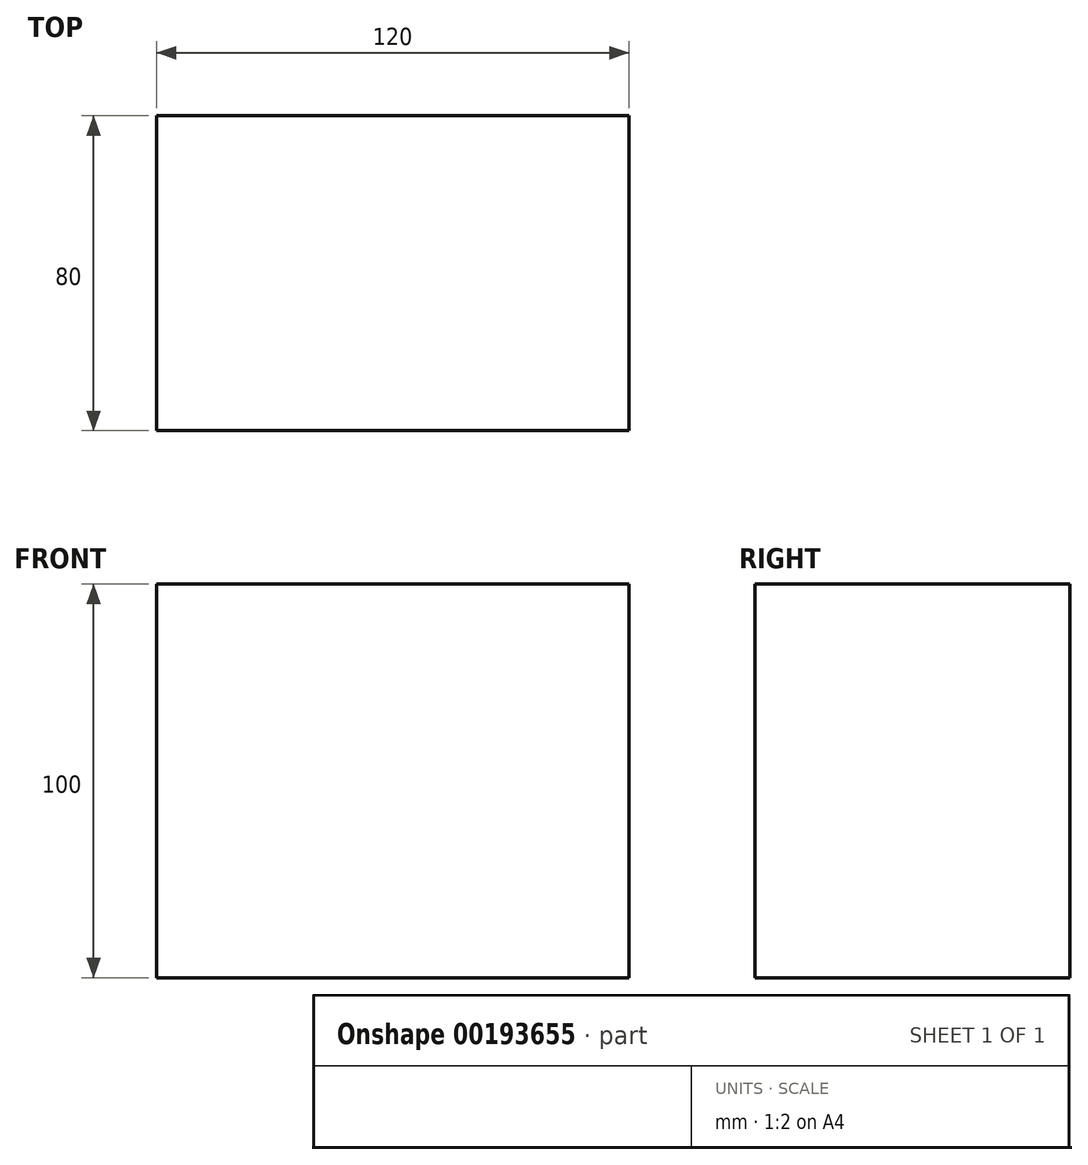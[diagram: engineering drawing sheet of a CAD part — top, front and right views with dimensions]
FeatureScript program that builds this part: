
annotation { "Feature Type Name" : "Feature", "Feature Type Description" : "" }
export const myFeature = defineFeature(function(context is Context, id is Id, definition is map)
    precondition{}
    {
        {
            var Q0;
            Q0=qCreatedBy(makeId("Top.planeOp"),FACE);
            var sketch = newSketch(context, id + "F0", { "sketchPlane" : qUnion([Q0])});
            skLineSegment(sketch, "E0.bottom", {"start": v(60, -40) * mm, "end": v(-60, -40) * mm});
            skLineSegment(sketch, "E0.top", {"start": v(60, 40) * mm, "end": v(-60, 40) * mm});
            skLineSegment(sketch, "E0.left", {"start": v(60, -40) * mm, "end": v(60, 40) * mm});
            skLineSegment(sketch, "E0.right", {"start": v(-60, -40) * mm, "end": v(-60, 40) * mm});
            skPoint(sketch, "E0.middle", {"position": v(0, 0) * mm});
            skSolve(sketch);
        }
        {
            var Q0;
            Q0 = qSketchRegion(id + "F0", true);
            extrude(context, id + "F1", {"entities" : qUnion([Q0]), "depth" : 100 * mm});
        }
        {
            var Q0;
            Q0=qCreatedBy(makeId("Top.planeOp"),FACE);
            var sketch = newSketch(context, id + "F2", { "sketchPlane" : qUnion([Q0])});
            skCircle(sketch, "E1", {"center": v(25.04, 0) * mm, "radius": 20.18 * mm});
            skSolve(sketch);
        }
        {
            var Q0;
            Q0 = qSketchRegion(id + "F2", true);
            extrude(context, id + "F3", {"entities" : qUnion([Q0]), "operationType" : NewBodyOperationType.REMOVE, "oppositeDirection" : true, "depth" : 80 * mm});
        }
    });
